# Revit family: ProVista™ Sashless Double Hung Window- SFS FSS SSF FSF
name_source: partatom
category: Windows
units: mm (PartAtom-declared; Revit-internal decimal feet)

## family parameters
Always vertical = Yes
Cut with Voids When Loaded = No
Host = Wall
OmniClass Number = 23.30.20.00
OmniClass Title = Windows
Room Calculation Point = No
Shared = No

## types (2) — shared parameters
BOT PANEL POSITION = 51.5 mm
Default Sill Height = 900 mm  [stored 2.95276 ft]
FRAME THICKNESS = 101.6 mm
Manufacturer = ALSPEC
Model = ProVista™ Sashless Double Hung Window- SFS FSS SSF FSF
SINGLE GLAZED THICKNESS = 6 mm  [stored 0.019685 ft]
Wall Closure = By host
X1 = 100 mm  [stored 0.328084 ft]
YEAR = 2022
zero-valued in all types: Height, Rough Height, Rough Width, TOLERANCE, Width

## per-type parameters (varying)
| type | URL |
| TYPICAL | WWW.ALSPEC.COM.AU |
| SFS | https://www.alspec.com.au |

note: [stored X ft] marks values corroborated as IEEE doubles in the binary element streams (Revit-internal decimal feet)

## geometry (parser evidence)
native form markers: Sweep x10
no freeform markers — native parametric forms only
